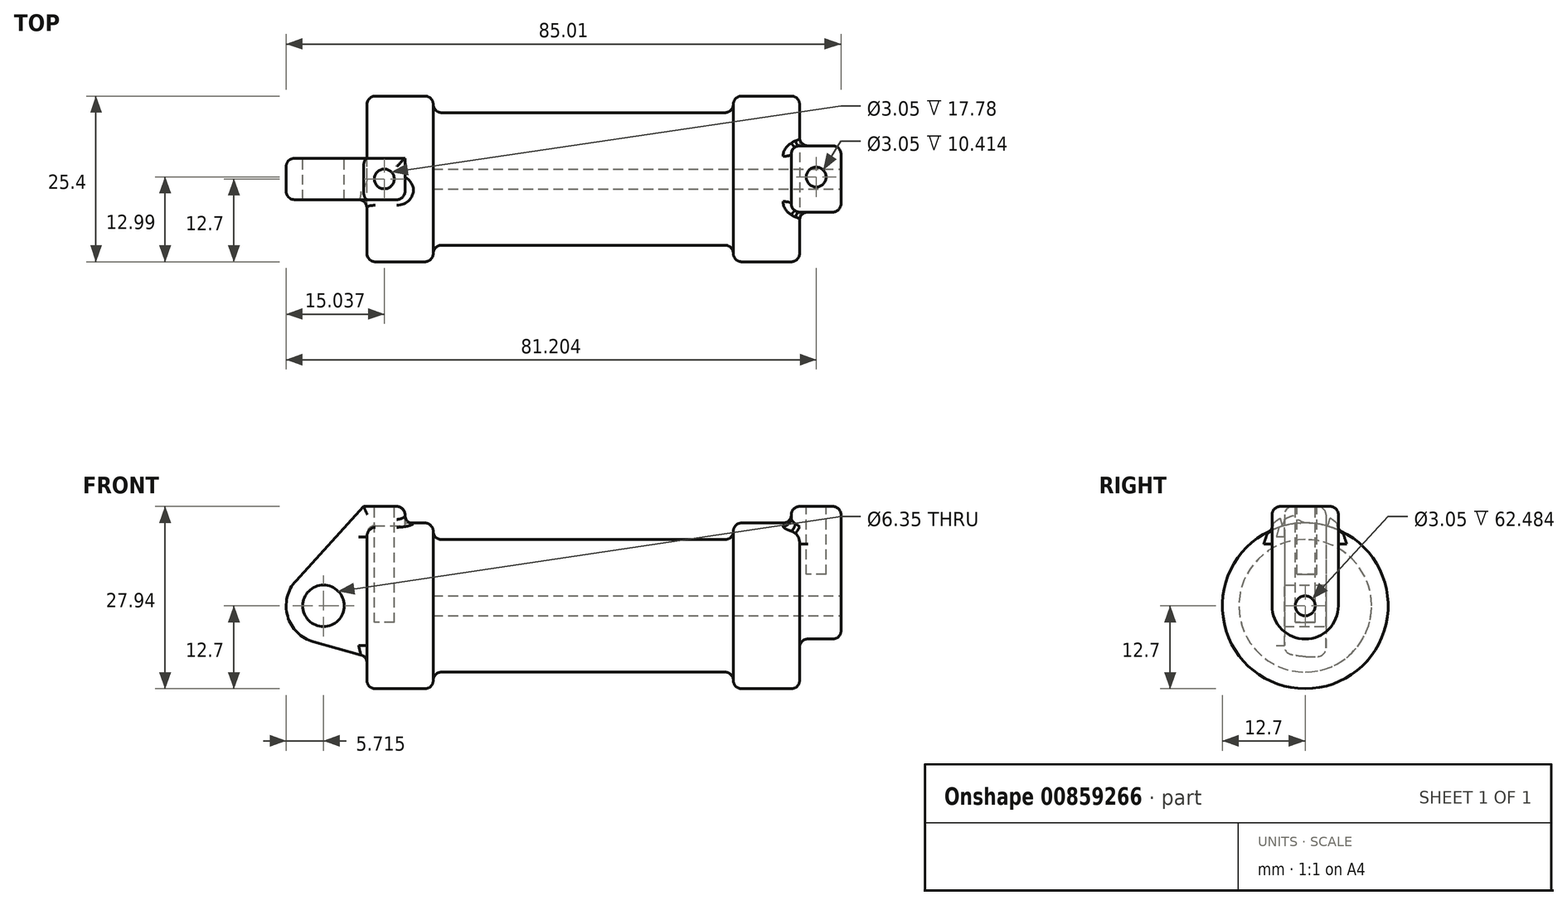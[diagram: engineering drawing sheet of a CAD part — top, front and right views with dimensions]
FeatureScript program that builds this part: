
annotation { "Feature Type Name" : "Feature", "Feature Type Description" : "" }
export const myFeature = defineFeature(function(context is Context, id is Id, definition is map)
    precondition{}
    {
        {
            var Q0;
            Q0=qCreatedBy(makeId("Front.planeOp"),FACE);
            var sketch = newSketch(context, id + "F0", { "sketchPlane" : qUnion([Q0])});
            skLineSegment(sketch, "E0", {"start": v(0, 0) * mm, "end": v(0, 12.7) * mm});
            skLineSegment(sketch, "E1", {"start": v(0, 12.7) * mm, "end": v(10.16, 12.7) * mm});
            skLineSegment(sketch, "E2", {"start": v(10.16, 12.7) * mm, "end": v(10.16, 10.16) * mm});
            skLineSegment(sketch, "E3", {"start": v(10.16, 10.16) * mm, "end": v(56.13, 10.16) * mm});
            skLineSegment(sketch, "E4", {"start": v(56.13, 10.16) * mm, "end": v(56.13, 12.7) * mm});
            skLineSegment(sketch, "E5", {"start": v(56.13, 12.7) * mm, "end": v(66.3, 12.7) * mm});
            skLineSegment(sketch, "E6", {"start": v(66.3, 12.7) * mm, "end": v(66.3, 0) * mm});
            skLineSegment(sketch, "E7", {"start": v(66.3, 0) * mm, "end": v(0, 0) * mm});
            skLineSegment(sketch, "E8", {"start": v(5.84, 15.24) * mm, "end": v(-0.5, 15.24) * mm});
            skLineSegment(sketch, "E9", {"start": v(-0.5, 15.24) * mm, "end": v(-10.88, 3.85) * mm});
            skLineSegment(sketch, "E10", {"start": v(0, 0) * mm, "end": v(-6.65, 0) * mm});
            skCircle(sketch, "E11", {"center": v(-6.65, 0) * mm, "radius": 5.72 * mm});
            skCircle(sketch, "E12", {"center": v(-6.65, 0) * mm, "radius": 3.18 * mm});
            skLineSegment(sketch, "E13", {"start": v(5.84, 15.24) * mm, "end": v(5.84, -9.4) * mm});
            skLineSegment(sketch, "E14", {"start": v(5.84, -9.4) * mm, "end": v(-8.18, -5.5) * mm});
            skSolve(sketch);
        }
        {
            var Q0;
            {var subQ0=sQuery(id+"F0.wireOp",EDGE,"E0");Q0=makeQuery(id+"F0.imprint","IMPRINT",FACE,{"disambiguationData":[TD([[makeQuery(id+"F0.imprint","IMPRINT",EDGE,{"derivedFrom":subQ0}),-1.0]])]});}
            var Q1;
            {var subQ0=sQuery(id+"F0.wireOp",EDGE,"E2");Q1=makeQuery(id+"F0.imprint","IMPRINT",FACE,{"disambiguationData":[TD([[makeQuery(id+"F0.imprint","IMPRINT",EDGE,{"derivedFrom":subQ0}),-1.0]])]});}
            var Q2;
            Q2=sQuery(id+"F0.wireOp",EDGE,"E7");
            revolve(context, id + "F1", {"surfaceOperationType" : NewSurfaceOperationType.NEW, "entities" : qUnion([Q0, Q1]), "axis" : qUnion([Q2]), "revolveType" : RevolveType.FULL});
        }
        {
            var Q0;
            {var subQ0=sQuery(id+"F0.wireOp",EDGE,"E0");Q0=makeQuery(id+"F0.imprint","IMPRINT",FACE,{"disambiguationData":[TD([[makeQuery(id+"F0.imprint","IMPRINT",EDGE,{"derivedFrom":subQ0}),-1.0]])]});}
            var Q1;
            {var subQ1=sQuery(id+"F0.wireOp",EDGE,"E0");Q1=makeQuery(id+"F0.imprint","IMPRINT",FACE,{"disambiguationData":[TD([[makeQuery(id+"F0.imprint","IMPRINT",EDGE,{"derivedFrom":subQ1}),1.0]])]});}
            var Q2;
            {var subQ0=sQuery(id+"F0.wireOp",EDGE,"E14");Q2=makeQuery(id+"F0.imprint","IMPRINT",FACE,{"disambiguationData":[TD([[makeQuery(id+"F0.imprint","IMPRINT",EDGE,{"derivedFrom":subQ0}),-1.0]])]});}
            var Q3;
            {var subQ5=sQuery(id+"F0.wireOp",EDGE,"E12");Q3=makeQuery(id+"F0.imprint","IMPRINT",FACE,{"disambiguationData":[TD([[makeQuery(id+"F0.imprint","IMPRINT",EDGE,{"derivedFrom":subQ5}),-1.0]])]});}
            extrude(context, id + "F2", {"entities" : qUnion([Q0, Q1, Q2, Q3]), "operationType" : NewBodyOperationType.ADD, "endBound" : BoundingType.SYMMETRIC, "depth" : 6.35 * mm, "offsetDistance" : 25.4 * mm, "hasSecondDirection" : true, "secondDirectionOppositeDirection" : true, "secondDirectionDepth" : 3.17 * mm});
        }
        {
            var Q0;
            Q0=makeQuery(id+"F1.opRevolve","SWEPT_FACE",FACE,{"disambiguationData":[OSD([sQuery(id+"F0.wireOp",EDGE,"E6")])]});
            var sketch = newSketch(context, id + "F3", { "sketchPlane" : qUnion([Q0])});
            skCircle(sketch, "E15", {"center": v(0, 0) * mm, "radius": 1.52 * mm});
            skCircle(sketch, "E16", {"center": v(0, 0) * mm, "radius": 5.08 * mm});
            skLineSegment(sketch, "E17", {"start": v(-5.08, 0) * mm, "end": v(-5.08, 15.24) * mm});
            skLineSegment(sketch, "E18", {"start": v(-5.08, 15.24) * mm, "end": v(5.08, 15.24) * mm});
            skLineSegment(sketch, "E19", {"start": v(5.08, 15.24) * mm, "end": v(5.08, 0) * mm});
            skSolve(sketch);
        }
        {
            var Q0;
            {var subQ0=sQuery(id+"F3.wireOp",EDGE,"E18");Q0=makeQuery(id+"F3.imprint","IMPRINT",FACE,{"disambiguationData":[TD([[makeQuery(id+"F3.imprint","IMPRINT",EDGE,{"derivedFrom":subQ0}),-1.0]])]});}
            var Q1;
            {var subQ0=sQuery(id+"F3.wireOp",EDGE,"E17");var subQ1=sQuery(id+"F3.wireOp",EDGE,"E16");var subQ2=makeQuery(id+"F3.imprint","INTERSECT",VERTEX,{"derivedFrom":[subQ1,subQ0]});Q1=makeQuery(id+"F3.imprint","IMPRINT",FACE,{"disambiguationData":[TD([[makeQuery(id+"F3.imprint","IMPRINT",EDGE,{"disambiguationData":[TD([[subQ2,1.0]])],"derivedFrom":subQ1}),-1.0]])]});}
            var Q2;
            Q2=makeQuery(id+"F3.imprint","IMPRINT",FACE,{"disambiguationData":[TD([[makeQuery(id+"F3.imprint","IMPRINT",EDGE,{"derivedFrom":sQuery(id+"F3.wireOp",EDGE,"E15")}),-1.0]])]});
            extrude(context, id + "F4", {"entities" : qUnion([Q0, Q1, Q2]), "operationType" : NewBodyOperationType.ADD, "oppositeDirection" : true, "depth" : 1.27 * mm, "offsetDistance" : 25.4 * mm, "hasSecondDirection" : true, "secondDirectionOppositeDirection" : false, "secondDirectionDepth" : 6.35 * mm});
        }
        {
            var Q0;
            Q0=makeQuery(id+"F3.imprint","IMPRINT",FACE,{"disambiguationData":[TD([[makeQuery(id+"F3.imprint","IMPRINT",EDGE,{"derivedFrom":sQuery(id+"F3.wireOp",EDGE,"E15")}),1.0]])]});
            var Q1;
            Q1=makeQuery(id+"F1.opRevolve","SWEPT_FACE",FACE,{"disambiguationData":[OSD([sQuery(id+"F0.wireOp",EDGE,"E2")])]});
            extrude(context, id + "F5", {"entities" : qUnion([Q0]), "operationType" : NewBodyOperationType.REMOVE, "endBound" : BoundingType.UP_TO_SURFACE, "oppositeDirection" : true, "depth" : 25.4 * mm, "endBoundEntityFace" : qUnion([Q1]), "offsetDistance" : 25.4 * mm});
        }
        {
            var Q0;
            Q0=makeQuery(id+"F2.opExtrude","SWEPT_FACE",FACE,{"disambiguationData":[OSD([sQuery(id+"F0.wireOp",EDGE,"E8")])]});
            var sketch = newSketch(context, id + "F6", { "sketchPlane" : qUnion([Q0])});
            skCircle(sketch, "E20", {"center": v(2.67, 0) * mm, "radius": 1.52 * mm});
            skSolve(sketch);
        }
        {
            var Q0;
            Q0 = qSketchRegion(id + "F6", true);
            extrude(context, id + "F7", {"entities" : qUnion([Q0]), "operationType" : NewBodyOperationType.REMOVE, "oppositeDirection" : true, "depth" : 17.78 * mm, "offsetDistance" : 25.4 * mm});
        }
        {
            var Q0;
            Q0=makeQuery(id+"F4.opExtrude","SWEPT_FACE",FACE,{"disambiguationData":[OSD([sQuery(id+"F3.wireOp",EDGE,"E18")])]});
            var sketch = newSketch(context, id + "F8", { "sketchPlane" : qUnion([Q0])});
            skCircle(sketch, "E21", {"center": v(68.83, 0.3) * mm, "radius": 1.52 * mm});
            skSolve(sketch);
        }
        {
            var Q0;
            Q0 = qSketchRegion(id + "F8", true);
            extrude(context, id + "F9", {"entities" : qUnion([Q0]), "operationType" : NewBodyOperationType.REMOVE, "oppositeDirection" : true, "depth" : 10.4 * mm, "offsetDistance" : 25.4 * mm});
        }
        {
            var Q0;
            Q0=makeQuery(id+"F1.opRevolve","SWEPT_EDGE",EDGE,{"disambiguationData":[OSD([sQuery(id+"F0.wireOp",EDGE,"E0"),sQuery(id+"F0.wireOp",EDGE,"E1")])]});
            var Q1;
            Q1=makeQuery(id+"F1.opRevolve","SWEPT_EDGE",EDGE,{"disambiguationData":[OSD([sQuery(id+"F0.wireOp",EDGE,"E1"),sQuery(id+"F0.wireOp",EDGE,"E2")])]});
            var Q2;
            Q2=makeQuery(id+"F1.opRevolve","SWEPT_EDGE",EDGE,{"disambiguationData":[OSD([sQuery(id+"F0.wireOp",EDGE,"E2"),sQuery(id+"F0.wireOp",EDGE,"E3")])]});
            var Q3;
            Q3=makeQuery(id+"F1.opRevolve","SWEPT_EDGE",EDGE,{"disambiguationData":[OSD([sQuery(id+"F0.wireOp",EDGE,"E3"),sQuery(id+"F0.wireOp",EDGE,"E4")])]});
            var Q4;
            Q4=makeQuery(id+"F1.opRevolve","SWEPT_EDGE",EDGE,{"disambiguationData":[OSD([sQuery(id+"F0.wireOp",EDGE,"E4"),sQuery(id+"F0.wireOp",EDGE,"E5")])]});
            var Q5;
            Q5=makeQuery(id+"F1.opRevolve","SWEPT_EDGE",EDGE,{"disambiguationData":[OSD([sQuery(id+"F0.wireOp",EDGE,"E5"),sQuery(id+"F0.wireOp",EDGE,"E6")])]});
            fillet(context, id + "F10", {"entities" : qUnion([Q0, Q1, Q2, Q3, Q4, Q5]), "radius" : 1.27 * mm, "tangentPropagation" : true, "allowEdgeOverflow" : false});
        }
        {
            var Q0;
            Q0=makeQuery(id+"F2.opExtrude","CAP_EDGE",EDGE,{"disambiguationData":[OSD([sQuery(id+"F0.wireOp",EDGE,"E13")])],"isStart":false});
            var Q1;
            Q1=makeQuery(id+"F2.boolean.opBoolean","INTERSECT",EDGE,{"derivedFrom":[makeQuery(id+"F1.opRevolve","SWEPT_FACE",FACE,{"disambiguationData":[OSD([sQuery(id+"F0.wireOp",EDGE,"E1")])]}),makeQuery(id+"F2.opExtrude","CAP_FACE",FACE,{"disambiguationData":[OSD([sQuery(id+"F0.wireOp",EDGE,"E8"),sQuery(id+"F0.wireOp",EDGE,"E9"),sQuery(id+"F0.wireOp",EDGE,"E11"),sQuery(id+"F0.wireOp",EDGE,"E12"),sQuery(id+"F0.wireOp",EDGE,"E13"),sQuery(id+"F0.wireOp",EDGE,"E14")])],"isStart":false})]});
            var Q2;
            Q2=makeQuery(id+"F2.opExtrude","SWEPT_EDGE",EDGE,{"disambiguationData":[OSD([sQuery(id+"F0.wireOp",EDGE,"E8"),sQuery(id+"F0.wireOp",EDGE,"E13")])]});
            var Q3;
            Q3=makeQuery(id+"F2.opExtrude","CAP_EDGE",EDGE,{"disambiguationData":[OSD([sQuery(id+"F0.wireOp",EDGE,"E8")])],"isStart":false});
            var Q4;
            Q4=makeQuery(id+"F2.opExtrude","CAP_EDGE",EDGE,{"disambiguationData":[OSD([sQuery(id+"F0.wireOp",EDGE,"E8")])],"isStart":true});
            var Q5;
            Q5=makeQuery(id+"F2.opExtrude","CAP_EDGE",EDGE,{"disambiguationData":[OSD([sQuery(id+"F0.wireOp",EDGE,"E9")])],"isStart":false});
            var Q6;
            Q6=makeQuery(id+"F2.opExtrude","CAP_EDGE",EDGE,{"disambiguationData":[OSD([sQuery(id+"F0.wireOp",EDGE,"E9")])],"isStart":true});
            fillet(context, id + "F11", {"entities" : qUnion([Q0, Q1, Q2, Q3, Q4, Q5, Q6]), "radius" : 1.27 * mm, "tangentPropagation" : true, "allowEdgeOverflow" : false});
        }
        {
            var Q0;
            Q0=makeQuery(id+"F4.boolean.opBoolean","INTERSECT",EDGE,{"derivedFrom":[makeQuery(id+"F1.opRevolve","SWEPT_FACE",FACE,{"disambiguationData":[OSD([sQuery(id+"F0.wireOp",EDGE,"E6")])]}),makeQuery(id+"F4.opExtrude","SWEPT_FACE",FACE,{"disambiguationData":[OSD([sQuery(id+"F3.wireOp",EDGE,"E17")])]})]});
            var Q1;
            Q1=makeQuery(id+"F4.opExtrude","CAP_EDGE",EDGE,{"disambiguationData":[OSD([sQuery(id+"F3.wireOp",EDGE,"E17")])],"isStart":true});
            var Q2;
            Q2=makeQuery(id+"F4.opExtrude","SWEPT_EDGE",EDGE,{"disambiguationData":[OSD([sQuery(id+"F3.wireOp",EDGE,"E18"),sQuery(id+"F3.wireOp",EDGE,"E19")])]});
            var Q3;
            Q3=makeQuery(id+"F4.opExtrude","CAP_EDGE",EDGE,{"disambiguationData":[OSD([sQuery(id+"F3.wireOp",EDGE,"E18")])],"isStart":true});
            var Q4;
            Q4=makeQuery(id+"F4.opExtrude","SWEPT_EDGE",EDGE,{"disambiguationData":[OSD([sQuery(id+"F3.wireOp",EDGE,"E17"),sQuery(id+"F3.wireOp",EDGE,"E18")])]});
            var Q5;
            Q5=makeQuery(id+"F4.opExtrude","CAP_EDGE",EDGE,{"disambiguationData":[OSD([sQuery(id+"F3.wireOp",EDGE,"E18")])],"isStart":false});
            var Q6;
            Q6=makeQuery(id+"F4.boolean.opBoolean","INTERSECT",EDGE,{"derivedFrom":[makeQuery(id+"F1.opRevolve","SWEPT_FACE",FACE,{"disambiguationData":[OSD([sQuery(id+"F0.wireOp",EDGE,"E5")])]}),makeQuery(id+"F4.opExtrude","CAP_FACE",FACE,{"disambiguationData":[OSD([sQuery(id+"F3.wireOp",EDGE,"E15"),sQuery(id+"F3.wireOp",EDGE,"E16"),sQuery(id+"F3.wireOp",EDGE,"E17"),sQuery(id+"F3.wireOp",EDGE,"E18"),sQuery(id+"F3.wireOp",EDGE,"E19")])],"isStart":false})]});
            var Q7;
            Q7=makeQuery(id+"F4.opExtrude","CAP_EDGE",EDGE,{"disambiguationData":[OSD([sQuery(id+"F3.wireOp",EDGE,"E17")])],"isStart":false});
            var Q8;
            Q8=makeQuery(id+"F4.opExtrude","CAP_EDGE",EDGE,{"disambiguationData":[OSD([sQuery(id+"F3.wireOp",EDGE,"E19")])],"isStart":false});
            fillet(context, id + "F12", {"entities" : qUnion([Q0, Q1, Q2, Q3, Q4, Q5, Q6, Q7, Q8]), "radius" : 1.27 * mm, "tangentPropagation" : true, "allowEdgeOverflow" : false});
        }
    });
